# Revit family: STH9952Q_30_40_65
name_source: partatom
category: Luminárias
units: mm (PartAtom-declared; Revit-internal decimal feet)

## family parameters
Compartilhado = Não
Corte com vazios quando carregada = Não
Cota do conector redondo = Utilizar diâmetro
Fonte luminosa = Sim
Hospedeiro = Forro
Manter orientação da anotação = Não
Número OmniClass = 23.80.70.11
Ponto de cálculo do ambiente = Não
Sempre na vertical = Sim
Tipo de parte = Normal
Título OmniClass = Luminaries for Internal Lighting

## types (3) — shared parameters
Altura = 0.03 m
Comprimento = 0.17 m
Dimerização = Não dimerizável
Estrutura = Al - Branco
Fabricante = Stella
Filtro de cor = 16777215
Fluxo Luminoso = 1100 lm
Grau de proteção (IP) = IP20
IRC (Índice de reprodução de cores) = >80
Largura = 0.17 m
Modelo = Painel de Embutir ECO
Potência = 12 W
Tensão Elétrica = 100V-240V
Troca de temperatura da cor de lâmpada com esmaecimento = <Nenhum>
URL = https://stella.com.br
Ângulo de Abertura = 120°
Ângulo de inclinação = 90.00°
zero-valued in all types: Elevação padrão

## per-type parameters (varying)
| type | Arquivo de rede fotométrica | Luminoso | Referência | Temperatura da cor (K) |
| STH9952Q/30 - BIVOLT - 3000K - 1100lm - 120° | STELLA - STH9952Q-30 - PAINEL DE EMBUTIR ECO 12W.ies | Luminoso - 3000K | STH9952Q/30 - BIVOLT | 3000 K |
| STH9952Q/40 - BIVOLT - 4000K - 1100lm - 120° | STELLA - STH9952Q-40 - PAINEL DE EMBUTIR ECO 12W.ies | Luminoso - 4000K | STH9952Q/40 - BIVOLT | 4000 K |
| STH9952Q/65 - BIVOLT - 6500K - 1100lm - 120° | STELLA - STH9952Q-65 - PAINEL DE EMBUTIR ECO 12W.ies | Luminoso - 6500K | STH9952Q/65 - BIVOLT | 6500 K |
